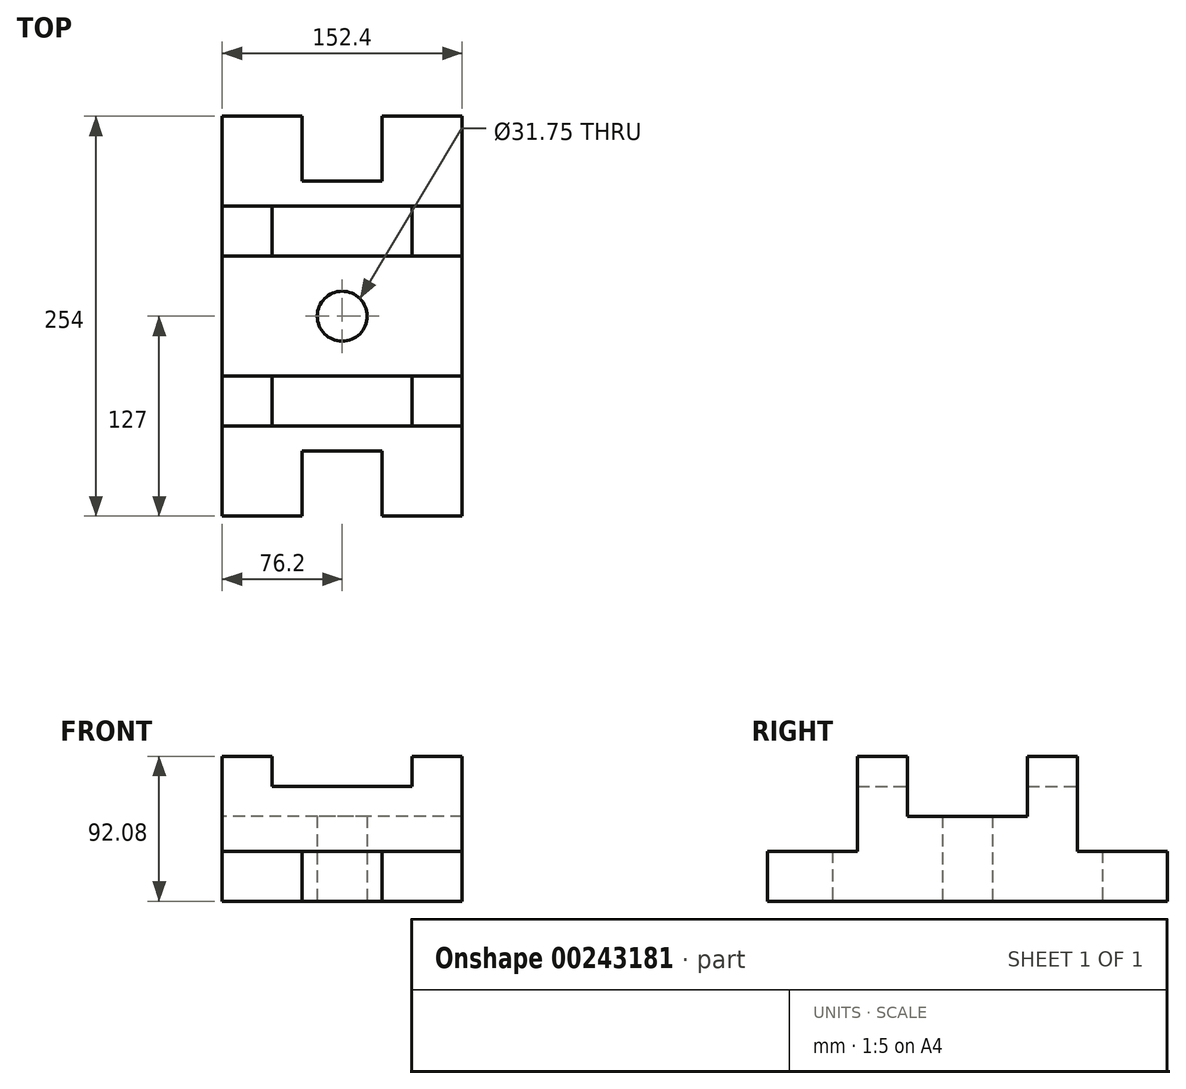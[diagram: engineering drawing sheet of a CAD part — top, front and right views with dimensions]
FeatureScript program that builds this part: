
annotation { "Feature Type Name" : "Feature", "Feature Type Description" : "" }
export const myFeature = defineFeature(function(context is Context, id is Id, definition is map)
    precondition{}
    {
        {
            var Q0;
            Q0=qCreatedBy(makeId("Top.planeOp"),FACE);
            var sketch = newSketch(context, id + "F0", { "sketchPlane" : qUnion([Q0])});
            skLineSegment(sketch, "E0", {"start": v(0, 0) * mm, "end": v(-50.8, 0) * mm});
            skLineSegment(sketch, "E1", {"start": v(-152.4, 0) * mm, "end": v(-152.4, 254) * mm});
            skLineSegment(sketch, "E2", {"start": v(-152.4, 254) * mm, "end": v(-101.6, 254) * mm});
            skLineSegment(sketch, "E3", {"start": v(0, 0) * mm, "end": v(0, 254) * mm});
            skLineSegment(sketch, "E4", {"start": v(-50.8, 254) * mm, "end": v(-50.8, 212.73) * mm});
            skLineSegment(sketch, "E5", {"start": v(-101.6, 254) * mm, "end": v(-101.6, 212.73) * mm});
            skLineSegment(sketch, "E6", {"start": v(-101.6, 41.27) * mm, "end": v(-50.8, 41.27) * mm});
            skPoint(sketch, "E7", {"position": v(-101.6, 41.27) * mm});
            skPoint(sketch, "E8", {"position": v(-50.8, 41.27) * mm});
            skPoint(sketch, "E9", {"position": v(-101.6, 0) * mm});
            skPoint(sketch, "E10", {"position": v(-50.8, 0) * mm});
            skLineSegment(sketch, "E11.MirrorCS", {"start": v(0, 254) * mm, "end": v(-50.8, 254) * mm});
            skPoint(sketch, "E12.MirrorP", {"position": v(-50.8, 254) * mm});
            skLineSegment(sketch, "E13.MirrorCS", {"start": v(-101.6, 212.73) * mm, "end": v(-50.8, 212.73) * mm});
            skPoint(sketch, "E14.MirrorP", {"position": v(-101.6, 212.73) * mm});
            skPoint(sketch, "E15.MirrorP", {"position": v(-50.8, 212.73) * mm});
            skPoint(sketch, "E16.MirrorP", {"position": v(-101.6, 254) * mm});
            skLineSegment(sketch, "E17.trimOffspring", {"start": v(-101.6, 0) * mm, "end": v(-152.4, 0) * mm});
            skPoint(sketch, "E18.orphan", {"position": v(-152.4, 41.27) * mm});
            skPoint(sketch, "E19.orphan", {"position": v(0, 41.28) * mm});
            skLineSegment(sketch, "E20.trimOffspring", {"start": v(-101.6, 254) * mm, "end": v(-152.4, 254) * mm});
            skLineSegment(sketch, "E21.trimOffspring", {"start": v(-50.8, 254) * mm, "end": v(0, 254) * mm});
            skLineSegment(sketch, "E22.trimOffspring", {"start": v(-101.6, 41.27) * mm, "end": v(-101.6, 0) * mm});
            skLineSegment(sketch, "E23.trimOffspring", {"start": v(-50.8, 41.28) * mm, "end": v(-50.8, 0) * mm});
            skLineSegment(sketch, "E24", {"start": v(-152.4, 196.85) * mm, "end": v(0, 196.85) * mm});
            skLineSegment(sketch, "E25", {"start": v(-152.4, 57.15) * mm, "end": v(0, 57.15) * mm});
            skPoint(sketch, "E26", {"position": v(-76.2, 127) * mm});
            skCircle(sketch, "E27", {"center": v(-76.2, 127) * mm, "radius": 15.88 * mm});
            skLineSegment(sketch, "E28", {"start": v(-152.4, 165.1) * mm, "end": v(0, 165.1) * mm});
            skLineSegment(sketch, "E29", {"start": v(-152.4, 88.9) * mm, "end": v(0, 88.9) * mm});
            skPoint(sketch, "E30.orphan", {"position": v(-76.2, 212.73) * mm});
            skPoint(sketch, "E31.start.orphan", {"position": v(-152.4, 127) * mm});
            skPoint(sketch, "E32.orphan", {"position": v(0, 127) * mm});
            skPoint(sketch, "E33.trimOffspring.end.orphan", {"position": v(-76.2, 41.27) * mm});
            skLineSegment(sketch, "E34", {"start": v(-120.65, 196.85) * mm, "end": v(-120.65, 165.1) * mm});
            skPoint(sketch, "E34.endSnap0", {"position": v(-76.2, 165.1) * mm});
            skLineSegment(sketch, "E35", {"start": v(-120.65, 88.9) * mm, "end": v(-120.65, 57.15) * mm});
            skLineSegment(sketch, "E36", {"start": v(-31.75, 196.85) * mm, "end": v(-31.75, 165.1) * mm});
            skLineSegment(sketch, "E37", {"start": v(-31.75, 88.9) * mm, "end": v(-31.75, 57.15) * mm});
            skSolve(sketch);
        }
        {
            var Q0;
            {var subQ0=sQuery(id+"F0.wireOp",EDGE,"E11.MirrorCS");var subQ1=sQuery(id+"F0.wireOp",EDGE,"E1");var subQ2=makeQuery(id+"F0.imprint","INTERSECT",VERTEX,{"derivedFrom":[subQ1,subQ0]});Q0=makeQuery(id+"F0.imprint","IMPRINT",FACE,{"disambiguationData":[TD([[makeQuery(id+"F0.imprint","IMPRINT",EDGE,{"disambiguationData":[TD([[subQ2,1.0]])],"derivedFrom":subQ1}),-1.0]])]});}
            var Q1;
            {var subQ0=sQuery(id+"F0.wireOp",EDGE,"k4FPTNfp-YAdw-mFhX-T3jj-mjTIoW7fOMzt");var subQ1=sQuery(id+"F0.wireOp",EDGE,"E1");var subQ2=makeQuery(id+"F0.imprint","INTERSECT",VERTEX,{"derivedFrom":[subQ1,subQ0]});Q1=makeQuery(id+"F0.imprint","IMPRINT",FACE,{"disambiguationData":[TD([[makeQuery(id+"F0.imprint","IMPRINT",EDGE,{"disambiguationData":[TD([[subQ2,-1.0]])],"derivedFrom":subQ1}),-1.0]])]});}
            var Q2;
            {var subQ0=sQuery(id+"F0.wireOp",EDGE,"E13.MirrorCS");var subQ1=sQuery(id+"F0.wireOp",EDGE,"E4");var subQ2=makeQuery(id+"F0.imprint","INTERSECT",VERTEX,{"derivedFrom":[subQ1,subQ0]});Q2=makeQuery(id+"F0.imprint","IMPRINT",FACE,{"disambiguationData":[TD([[makeQuery(id+"F0.imprint","IMPRINT",EDGE,{"disambiguationData":[TD([[subQ2,-1.0]])],"derivedFrom":subQ1}),-1.0]])]});}
            var Q3;
            {var subQ0=sQuery(id+"F0.wireOp",EDGE,"k4FPTNfp-YAdw-mFhX-T3jj-mjTIoW7fOMzt");var subQ1=sQuery(id+"F0.wireOp",EDGE,"E4");var subQ2=makeQuery(id+"F0.imprint","INTERSECT",VERTEX,{"derivedFrom":[subQ1,subQ0]});Q3=makeQuery(id+"F0.imprint","IMPRINT",FACE,{"disambiguationData":[TD([[makeQuery(id+"F0.imprint","IMPRINT",EDGE,{"disambiguationData":[TD([[subQ2,-1.0]])],"derivedFrom":subQ1}),-1.0]])]});}
            var Q4;
            {var subQ0=sQuery(id+"F0.wireOp",EDGE,"E6");var subQ1=sQuery(id+"F0.wireOp",EDGE,"E1");var subQ2=makeQuery(id+"F0.imprint","INTERSECT",VERTEX,{"derivedFrom":[subQ1,subQ0]});Q4=makeQuery(id+"F0.imprint","IMPRINT",FACE,{"disambiguationData":[TD([[makeQuery(id+"F0.imprint","IMPRINT",EDGE,{"disambiguationData":[TD([[subQ2,-1.0]])],"derivedFrom":subQ1}),-1.0]])]});}
            var Q5;
            {var subQ0=sQuery(id+"F0.wireOp",EDGE,"E1");var subQ1=sQuery(id+"F0.wireOp",EDGE,"E0");var subQ2=makeQuery(id+"F0.imprint","INTERSECT",VERTEX,{"derivedFrom":[subQ1,subQ0]});Q5=makeQuery(id+"F0.imprint","IMPRINT",FACE,{"disambiguationData":[TD([[makeQuery(id+"F0.imprint","IMPRINT",EDGE,{"disambiguationData":[TD([[subQ2,1.0]])],"derivedFrom":subQ1}),-1.0]])]});}
            var Q6;
            {var subQ0=sQuery(id+"F0.wireOp",EDGE,"E6");var subQ1=sQuery(id+"F0.wireOp",EDGE,"E3");var subQ2=makeQuery(id+"F0.imprint","INTERSECT",VERTEX,{"derivedFrom":[subQ1,subQ0]});Q6=makeQuery(id+"F0.imprint","IMPRINT",FACE,{"disambiguationData":[TD([[makeQuery(id+"F0.imprint","IMPRINT",EDGE,{"disambiguationData":[TD([[subQ2,-1.0]])],"derivedFrom":subQ1}),1.0]])]});}
            var Q7;
            {var subQ0=sQuery(id+"F0.wireOp",EDGE,"E3");var subQ1=sQuery(id+"F0.wireOp",EDGE,"E0");var subQ2=makeQuery(id+"F0.imprint","INTERSECT",VERTEX,{"derivedFrom":[subQ1,subQ0]});Q7=makeQuery(id+"F0.imprint","IMPRINT",FACE,{"disambiguationData":[TD([[makeQuery(id+"F0.imprint","IMPRINT",EDGE,{"disambiguationData":[TD([[subQ2,-1.0]])],"derivedFrom":subQ1}),-1.0]])]});}
            var Q8;
            {var subQ0=sQuery(id+"F0.wireOp",EDGE,"k4FPTNfp-YAdw-mFhX-T3jj-mjTIoW7fOMzt");var subQ1=sQuery(id+"F0.wireOp",EDGE,"E3");var subQ2=makeQuery(id+"F0.imprint","INTERSECT",VERTEX,{"derivedFrom":[subQ1,subQ0]});Q8=makeQuery(id+"F0.imprint","IMPRINT",FACE,{"disambiguationData":[TD([[makeQuery(id+"F0.imprint","IMPRINT",EDGE,{"disambiguationData":[TD([[subQ2,-1.0]])],"derivedFrom":subQ1}),1.0]])]});}
            var Q9;
            {var subQ0=sQuery(id+"F0.wireOp",EDGE,"E11.MirrorCS");var subQ1=sQuery(id+"F0.wireOp",EDGE,"E3");var subQ2=makeQuery(id+"F0.imprint","INTERSECT",VERTEX,{"derivedFrom":[subQ1,subQ0]});Q9=makeQuery(id+"F0.imprint","IMPRINT",FACE,{"disambiguationData":[TD([[makeQuery(id+"F0.imprint","IMPRINT",EDGE,{"disambiguationData":[TD([[subQ2,1.0]])],"derivedFrom":subQ1}),1.0]])]});}
            var Q10;
            Q10=makeQuery(id+"F0.imprint","IMPRINT",FACE,{"disambiguationData":[TD([[makeQuery(id+"F0.imprint","IMPRINT",EDGE,{"derivedFrom":sQuery(id+"F0.wireOp",EDGE,"E4")}),1.0]])]});
            var Q11;
            {var subQ0=sQuery(id+"F0.wireOp",EDGE,"E17.trimOffspring");Q11=makeQuery(id+"F0.imprint","IMPRINT",FACE,{"disambiguationData":[TD([[makeQuery(id+"F0.imprint","IMPRINT",EDGE,{"derivedFrom":subQ0}),-1.0]])]});}
            var Q12;
            {var subQ2=sQuery(id+"F0.wireOp",EDGE,"E5");Q12=makeQuery(id+"F0.imprint","IMPRINT",FACE,{"disambiguationData":[TD([[makeQuery(id+"F0.imprint","IMPRINT",EDGE,{"derivedFrom":subQ2}),-1.0]])]});}
            extrude(context, id + "F1", {"entities" : qUnion([Q0, Q1, Q2, Q3, Q4, Q5, Q6, Q7, Q8, Q9, Q10, Q11, Q12]), "depth" : 31.75 * mm});
        }
        {
            var Q0;
            {var subQ0=sQuery(id+"F0.wireOp",EDGE,"E24");Q0=makeQuery(id+"F0.imprint","IMPRINT",FACE,{"disambiguationData":[TD([[makeQuery(id+"F0.imprint","IMPRINT",EDGE,{"derivedFrom":subQ0}),-1.0]])]});}
            var Q1;
            {var subQ1=sQuery(id+"F0.wireOp",EDGE,"E1");var subQ5=sQuery(id+"F0.wireOp",EDGE,"E25");var subQ6=makeQuery(id+"F0.imprint","INTERSECT",VERTEX,{"derivedFrom":[subQ1,subQ5]});Q1=makeQuery(id+"F0.imprint","IMPRINT",FACE,{"disambiguationData":[TD([[makeQuery(id+"F0.imprint","IMPRINT",EDGE,{"disambiguationData":[TD([[subQ6,-1.0]])],"derivedFrom":subQ1}),-1.0]])]});}
            var Q2;
            {var subQ1=sQuery(id+"F0.wireOp",EDGE,"E3");var subQ6=sQuery(id+"F0.wireOp",EDGE,"E25");var subQ9=makeQuery(id+"F0.imprint","INTERSECT",VERTEX,{"derivedFrom":[subQ1,subQ6]});Q2=makeQuery(id+"F0.imprint","IMPRINT",FACE,{"disambiguationData":[TD([[makeQuery(id+"F0.imprint","IMPRINT",EDGE,{"disambiguationData":[TD([[subQ9,-1.0]])],"derivedFrom":subQ1}),1.0]])]});}
            var Q3;
            Q3=makeQuery(id+"F0.imprint","IMPRINT",FACE,{"disambiguationData":[TD([[makeQuery(id+"F0.imprint","IMPRINT",EDGE,{"derivedFrom":sQuery(id+"F0.wireOp",EDGE,"E27")}),-1.0]])]});
            extrude(context, id + "F2", {"entities" : qUnion([Q0, Q1, Q2, Q3]), "operationType" : NewBodyOperationType.ADD, "depth" : 53.97 * mm});
        }
        {
            var Q0;
            Q0=makeQuery(id+"F0.imprint","IMPRINT",FACE,{"disambiguationData":[TD([[makeQuery(id+"F0.imprint","IMPRINT",EDGE,{"derivedFrom":sQuery(id+"F0.wireOp",EDGE,"E27")}),1.0]])]});
            extrude(context, id + "F3", {"entities" : qUnion([Q0]), "operationType" : NewBodyOperationType.REMOVE, "oppositeDirection" : true, "depth" : 53.97 * mm});
        }
        {
            var Q0;
            {var subQ0=sQuery(id+"F0.wireOp",EDGE,"E24");Q0=makeQuery(id+"F0.imprint","IMPRINT",FACE,{"disambiguationData":[TD([[makeQuery(id+"F0.imprint","IMPRINT",EDGE,{"derivedFrom":subQ0}),-1.0]])]});}
            var Q1;
            {var subQ0=sQuery(id+"F0.wireOp",EDGE,"E25");Q1=makeQuery(id+"F0.imprint","IMPRINT",FACE,{"disambiguationData":[TD([[makeQuery(id+"F0.imprint","IMPRINT",EDGE,{"derivedFrom":subQ0}),1.0]])]});}
            extrude(context, id + "F4", {"entities" : qUnion([Q0, Q1]), "operationType" : NewBodyOperationType.ADD, "depth" : 73.02 * mm});
        }
        {
            var Q0;
            {var subQ5=sQuery(id+"F0.wireOp",EDGE,"E36");Q0=makeQuery(id+"F0.imprint","IMPRINT",FACE,{"disambiguationData":[TD([[makeQuery(id+"F0.imprint","IMPRINT",EDGE,{"derivedFrom":subQ5}),1.0]])]});}
            var Q1;
            {var subQ5=sQuery(id+"F0.wireOp",EDGE,"E37");Q1=makeQuery(id+"F0.imprint","IMPRINT",FACE,{"disambiguationData":[TD([[makeQuery(id+"F0.imprint","IMPRINT",EDGE,{"derivedFrom":subQ5}),1.0]])]});}
            var Q2;
            {var subQ5=sQuery(id+"F0.wireOp",EDGE,"E35");Q2=makeQuery(id+"F0.imprint","IMPRINT",FACE,{"disambiguationData":[TD([[makeQuery(id+"F0.imprint","IMPRINT",EDGE,{"derivedFrom":subQ5}),-1.0]])]});}
            var Q3;
            {var subQ5=sQuery(id+"F0.wireOp",EDGE,"E34");Q3=makeQuery(id+"F0.imprint","IMPRINT",FACE,{"disambiguationData":[TD([[makeQuery(id+"F0.imprint","IMPRINT",EDGE,{"derivedFrom":subQ5}),-1.0]])]});}
            extrude(context, id + "F5", {"entities" : qUnion([Q0, Q1, Q2, Q3]), "operationType" : NewBodyOperationType.ADD, "depth" : 92.07 * mm});
        }
    });
